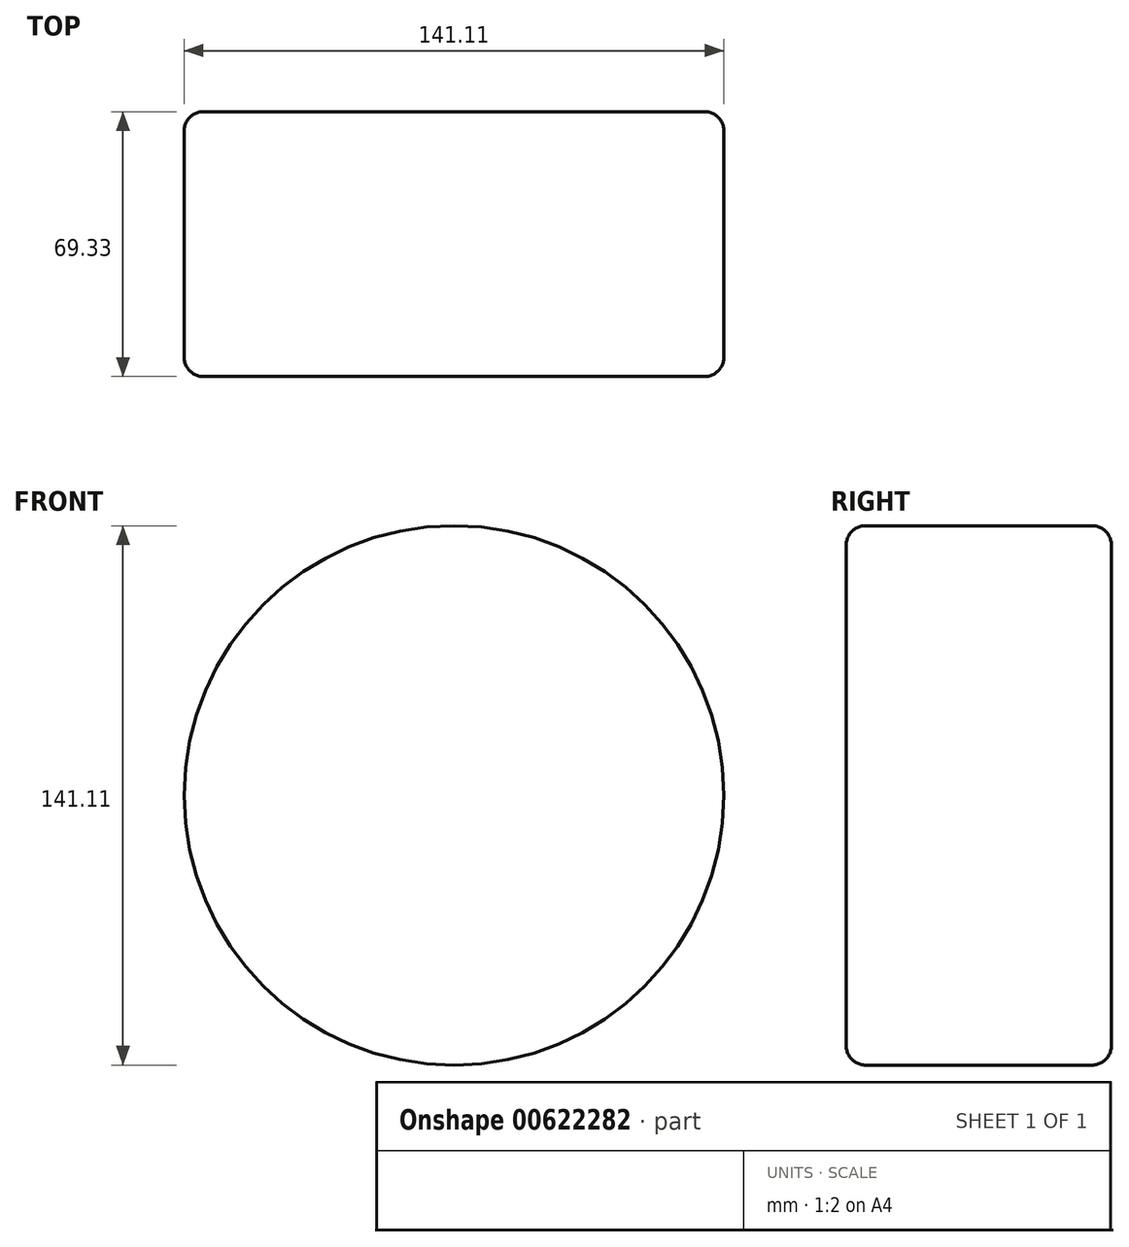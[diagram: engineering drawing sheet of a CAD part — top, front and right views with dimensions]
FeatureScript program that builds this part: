
annotation { "Feature Type Name" : "Feature", "Feature Type Description" : "" }
export const myFeature = defineFeature(function(context is Context, id is Id, definition is map)
    precondition{}
    {
        {
            var Q0;
            Q0=qCreatedBy(makeId("Front.planeOp"),FACE);
            var sketch = newSketch(context, id + "F0", { "sketchPlane" : qUnion([Q0])});
            skCircle(sketch, "E0", {"center": v(-48.53, -24.4) * mm, "radius": 70.56 * mm});
            skSolve(sketch);
        }
        {
            var Q0;
            Q0=makeQuery(id+"F0.imprint","IMPRINT",FACE,{"disambiguationData":[TD([[makeQuery(id+"F0.imprint","IMPRINT",EDGE,{"derivedFrom":sQuery(id+"F0.wireOp",EDGE,"E0")}),1.0]])]});
            extrude(context, id + "F1", {"entities" : qUnion([Q0]), "depth" : 69.33 * mm, "offsetDistance" : 25.4 * mm});
        }
        {
            var Q0;
            Q0=makeQuery(id+"F1.opExtrude","SWEPT_FACE",FACE,{"disambiguationData":[OSD([sQuery(id+"F0.wireOp",EDGE,"E0")])]});
            var Q1;
            Q1=makeQuery(id+"F1.opExtrude","CAP_EDGE",EDGE,{"disambiguationData":[OSD([sQuery(id+"F0.wireOp",EDGE,"E0")])],"isStart":false});
            fillet(context, id + "F2", {"entities" : qUnion([Q0, Q1]), "radius" : 5.08 * mm, "tangentPropagation" : true, "allowEdgeOverflow" : false});
        }
    });
